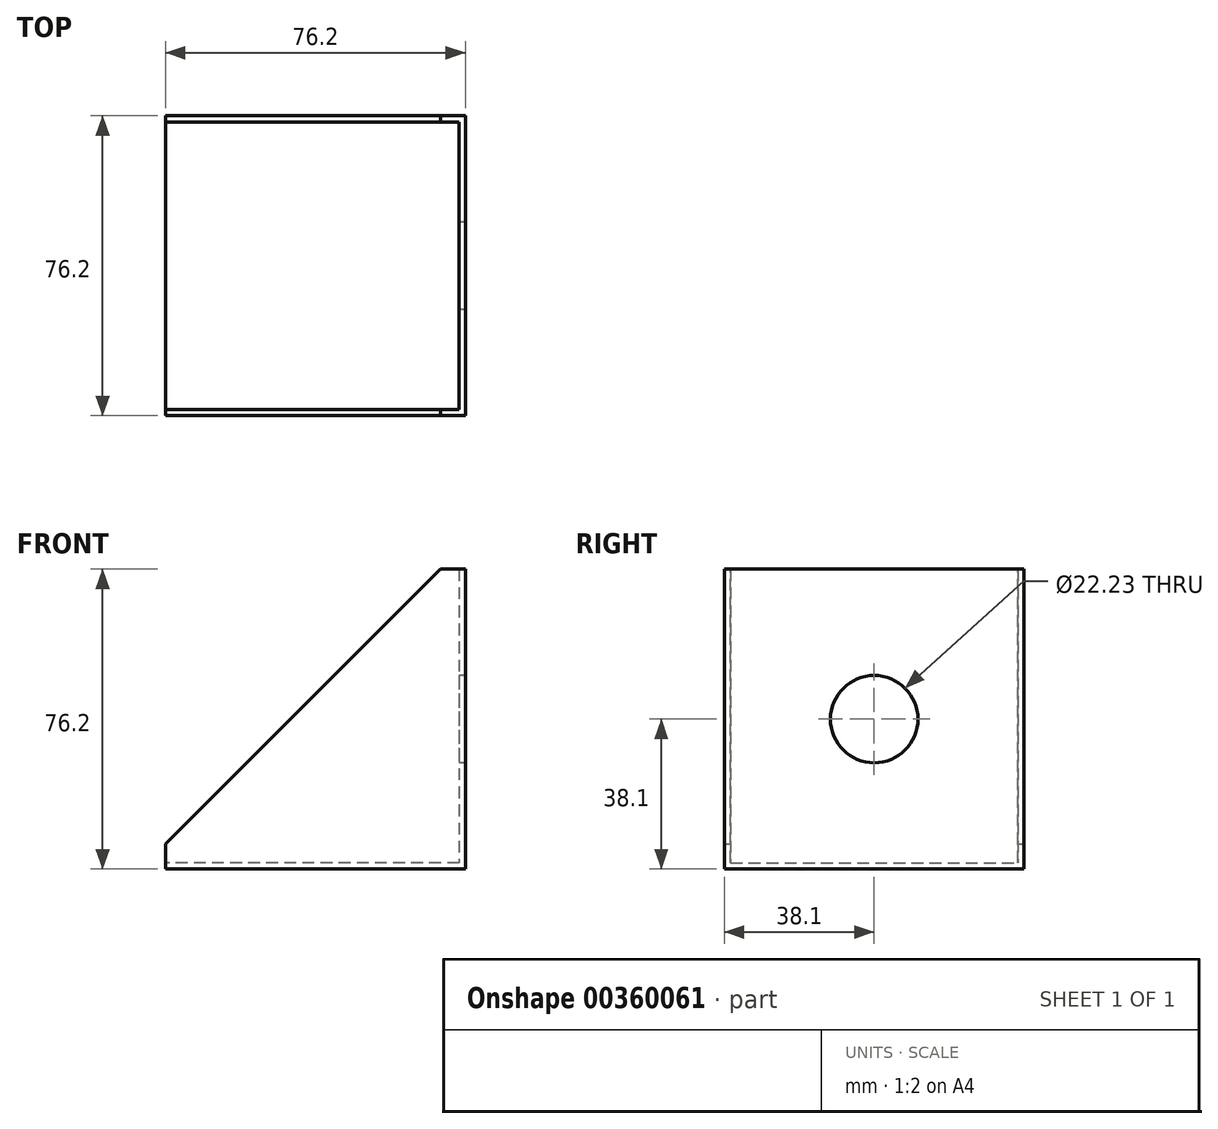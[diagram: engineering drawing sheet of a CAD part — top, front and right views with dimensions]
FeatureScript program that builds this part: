
annotation { "Feature Type Name" : "Feature", "Feature Type Description" : "" }
export const myFeature = defineFeature(function(context is Context, id is Id, definition is map)
    precondition{}
    {
        {
            var Q0;
            Q0=qCreatedBy(makeId("Front.planeOp"),FACE);
            var sketch = newSketch(context, id + "F0", { "sketchPlane" : qUnion([Q0])});
            skLineSegment(sketch, "E0", {"start": v(0, 0) * mm, "end": v(-76.2, 0) * mm});
            skLineSegment(sketch, "E1", {"start": v(-76.2, 0) * mm, "end": v(-76.2, 6.35) * mm});
            skLineSegment(sketch, "E2", {"start": v(-76.2, 6.35) * mm, "end": v(-6.35, 76.2) * mm});
            skLineSegment(sketch, "E3", {"start": v(-6.35, 76.2) * mm, "end": v(0, 76.2) * mm});
            skLineSegment(sketch, "E4", {"start": v(0, 76.2) * mm, "end": v(0, 0) * mm});
            skSolve(sketch);
        }
        {
            var Q0;
            Q0=makeQuery(id+"F0.imprint","IMPRINT",FACE,{"disambiguationData":[TD([[makeQuery(id+"F0.imprint","IMPRINT",EDGE,{"derivedFrom":sQuery(id+"F0.wireOp",EDGE,"E0")}),-1.0]])]});
            extrude(context, id + "F1", {"entities" : qUnion([Q0]), "depth" : 76.2 * mm});
        }
        {
            var Q0;
            Q0=makeQuery(id+"F1.opExtrude","SWEPT_FACE",FACE,{"disambiguationData":[OSD([sQuery(id+"F0.wireOp",EDGE,"E2")])]});
            var Q1;
            Q1=makeQuery(id+"F1.opExtrude","SWEPT_FACE",FACE,{"disambiguationData":[OSD([sQuery(id+"F0.wireOp",EDGE,"E1")])]});
            var Q2;
            Q2=makeQuery(id+"F1.opExtrude","SWEPT_FACE",FACE,{"disambiguationData":[OSD([sQuery(id+"F0.wireOp",EDGE,"E3")])]});
            shell(context, id + "F2", {"entities" : qUnion([Q0, Q1, Q2]), "thickness" : 1.59 * mm});
        }
        {
            var Q0;
            Q0=makeQuery(id+"F2.opShell","OFFSET_FACE",FACE,{"disambiguationData":[OSD([sQuery(id+"F0.wireOp",EDGE,"E4")])]});
            var sketch = newSketch(context, id + "F3", { "sketchPlane" : qUnion([Q0])});
            skCircle(sketch, "E5", {"center": v(38.1, 38.1) * mm, "radius": 11.11 * mm});
            skSolve(sketch);
        }
        {
            var Q0;
            Q0=makeQuery(id+"F3.imprint","IMPRINT",FACE,{"disambiguationData":[TD([[makeQuery(id+"F3.imprint","IMPRINT",EDGE,{"derivedFrom":sQuery(id+"F3.wireOp",EDGE,"E5")}),1.0]])]});
            extrude(context, id + "F4", {"entities" : qUnion([Q0]), "operationType" : NewBodyOperationType.REMOVE, "endBound" : BoundingType.THROUGH_ALL, "oppositeDirection" : true, "depth" : 25.4 * mm});
        }
    });
